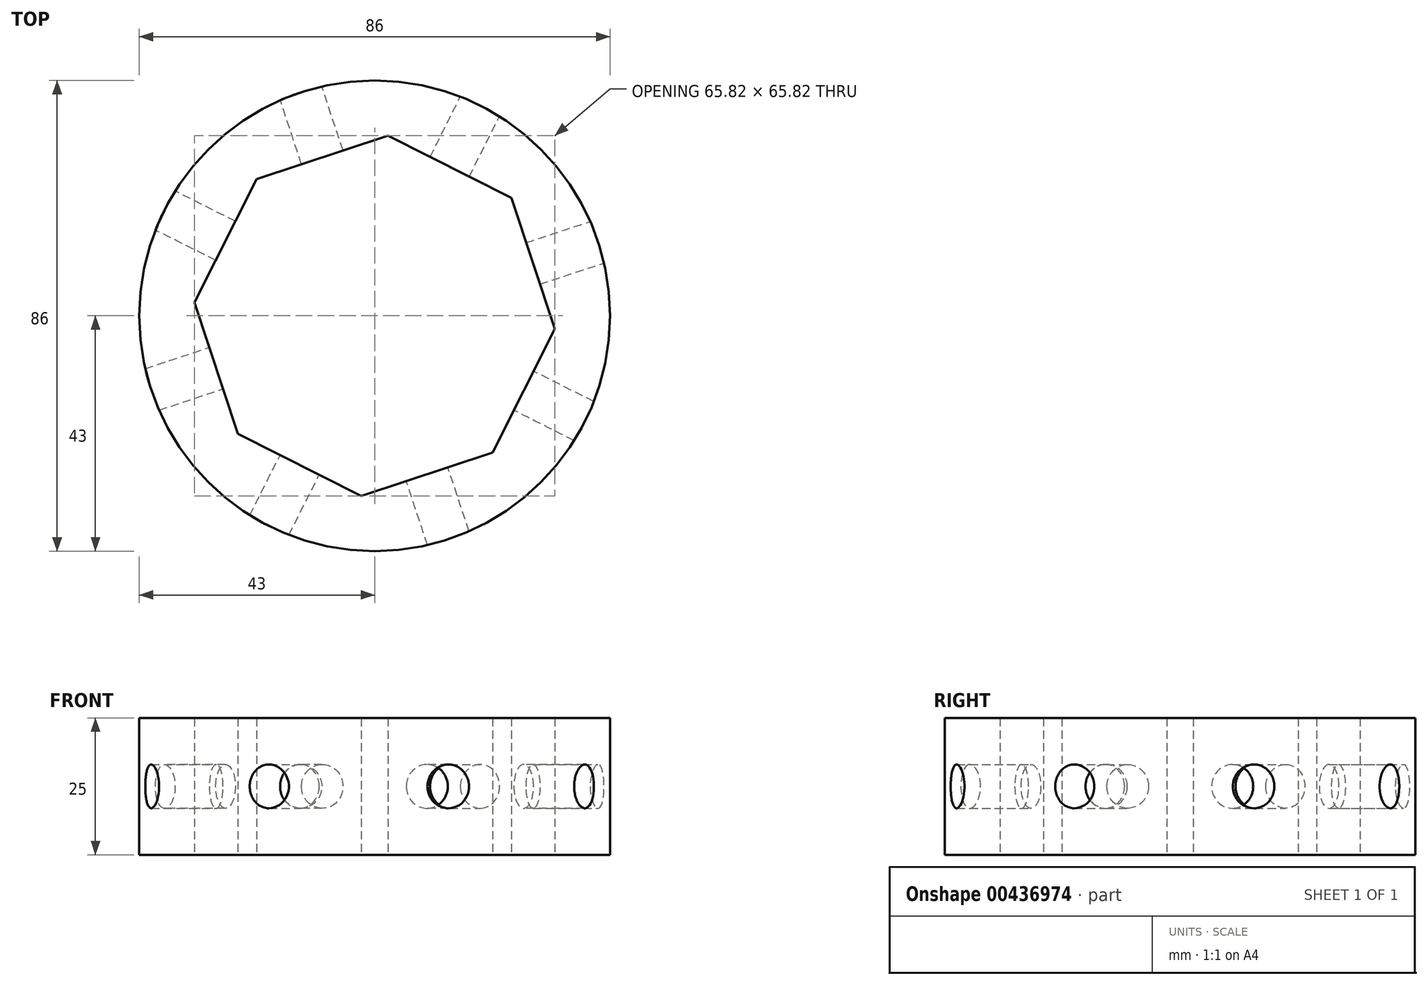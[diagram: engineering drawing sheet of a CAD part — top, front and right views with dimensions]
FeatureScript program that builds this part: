
annotation { "Feature Type Name" : "Feature", "Feature Type Description" : "" }
export const myFeature = defineFeature(function(context is Context, id is Id, definition is map)
    precondition{}
    {
        {
            var Q0;
            Q0=qCreatedBy(makeId("Top.planeOp"),FACE);
            var sketch = newSketch(context, id + "F0", { "sketchPlane" : qUnion([Q0])});
            skCircle(sketch, "E0", {"center": v(0, 0) * mm, "radius": 25 * mm, "construction": true});
            skCircle(sketch, "E1.cCircle", {"center": v(0, 0) * mm, "radius": 33 * mm, "construction": true});
            skLineSegment(sketch, "E1.0", {"start": v(-21.56, 24.98) * mm, "end": v(2.42, 32.91) * mm});
            skLineSegment(sketch, "E1.1", {"start": v(2.42, 32.91) * mm, "end": v(24.98, 21.56) * mm});
            skLineSegment(sketch, "E1.2", {"start": v(24.98, 21.56) * mm, "end": v(32.91, -2.42) * mm});
            skLineSegment(sketch, "E1.3", {"start": v(32.91, -2.42) * mm, "end": v(21.56, -24.98) * mm});
            skLineSegment(sketch, "E1.4", {"start": v(21.56, -24.98) * mm, "end": v(-2.42, -32.91) * mm});
            skLineSegment(sketch, "E1.5", {"start": v(-2.42, -32.91) * mm, "end": v(-24.98, -21.56) * mm});
            skLineSegment(sketch, "E1.6", {"start": v(-24.98, -21.56) * mm, "end": v(-32.91, 2.42) * mm});
            skLineSegment(sketch, "E1.7", {"start": v(-32.91, 2.42) * mm, "end": v(-21.56, 24.98) * mm});
            skCircle(sketch, "E2", {"center": v(0, 0) * mm, "radius": 43 * mm});
            skSolve(sketch);
        }
        {
            var Q0;
            Q0 = qSketchRegion(id + "F0", true);
            extrude(context, id + "F1", {"entities" : qUnion([Q0]), "depth" : 25 * mm, "offsetDistance" : 25 * mm});
        }
        {
            var Q0;
            Q0=makeQuery(id+"F1.opExtrude","SWEPT_FACE",FACE,{"disambiguationData":[OSD([sQuery(id+"F0.wireOp",EDGE,"E1.0")])]});
            var sketch = newSketch(context, id + "F2", { "sketchPlane" : qUnion([Q0])});
            skLineSegment(sketch, "E3.0.0", {"start": v(-12.63, 0) * mm, "end": v(12.63, 0) * mm, "construction": true});
            skLineSegment(sketch, "E3.0.1", {"start": v(12.63, 0) * mm, "end": v(12.63, 25) * mm, "construction": true});
            skLineSegment(sketch, "E3.0.2", {"start": v(12.63, 25) * mm, "end": v(-12.63, 25) * mm, "construction": true});
            skLineSegment(sketch, "E3.0.3", {"start": v(-12.63, 25) * mm, "end": v(-12.63, 0) * mm, "construction": true});
            skCircle(sketch, "E4", {"center": v(0, 12.5) * mm, "radius": 4 * mm});
            skPoint(sketch, "E4.centerSnap0", {"position": v(-12.63, 12.5) * mm});
            skPoint(sketch, "E4.centerSnap1", {"position": v(0, 25) * mm});
            skSolve(sketch);
        }
        {
            var Q0;
            Q0=makeQuery(id+"F1.opExtrude","SWEPT_FACE",FACE,{"disambiguationData":[OSD([sQuery(id+"F0.wireOp",EDGE,"E1.7")])]});
            var sketch = newSketch(context, id + "F3", { "sketchPlane" : qUnion([Q0])});
            skLineSegment(sketch, "E5.0.0", {"start": v(-12.63, 0) * mm, "end": v(12.63, 0) * mm, "construction": true});
            skLineSegment(sketch, "E5.0.1", {"start": v(12.63, 0) * mm, "end": v(12.63, 25) * mm, "construction": true});
            skLineSegment(sketch, "E5.0.2", {"start": v(12.63, 25) * mm, "end": v(-12.63, 25) * mm, "construction": true});
            skLineSegment(sketch, "E5.0.3", {"start": v(-12.63, 25) * mm, "end": v(-12.63, 0) * mm, "construction": true});
            skCircle(sketch, "E6", {"center": v(0, 12.5) * mm, "radius": 4 * mm});
            skPoint(sketch, "E6.centerSnap0", {"position": v(-12.63, 12.5) * mm});
            skPoint(sketch, "E6.centerSnap1", {"position": v(0, 25) * mm});
            skSolve(sketch);
        }
        {
            var Q0;
            Q0=makeQuery(id+"F1.opExtrude","SWEPT_FACE",FACE,{"disambiguationData":[OSD([sQuery(id+"F0.wireOp",EDGE,"E1.6")])]});
            var sketch = newSketch(context, id + "F4", { "sketchPlane" : qUnion([Q0])});
            skLineSegment(sketch, "E7.0.0", {"start": v(-12.63, 0) * mm, "end": v(12.63, 0) * mm, "construction": true});
            skLineSegment(sketch, "E7.0.1", {"start": v(12.63, 0) * mm, "end": v(12.63, 25) * mm, "construction": true});
            skLineSegment(sketch, "E7.0.2", {"start": v(12.63, 25) * mm, "end": v(-12.63, 25) * mm, "construction": true});
            skLineSegment(sketch, "E7.0.3", {"start": v(-12.63, 25) * mm, "end": v(-12.63, 0) * mm, "construction": true});
            skCircle(sketch, "E8", {"center": v(0, 12.5) * mm, "radius": 4 * mm});
            skPoint(sketch, "E8.centerSnap0", {"position": v(-12.63, 12.5) * mm});
            skPoint(sketch, "E8.centerSnap1", {"position": v(0, 25) * mm});
            skSolve(sketch);
        }
        {
            var Q0;
            Q0=makeQuery(id+"F1.opExtrude","SWEPT_FACE",FACE,{"disambiguationData":[OSD([sQuery(id+"F0.wireOp",EDGE,"E1.5")])]});
            var sketch = newSketch(context, id + "F5", { "sketchPlane" : qUnion([Q0])});
            skLineSegment(sketch, "E9.0.0", {"start": v(-12.63, 0) * mm, "end": v(12.63, 0) * mm, "construction": true});
            skLineSegment(sketch, "E9.0.1", {"start": v(12.63, 0) * mm, "end": v(12.63, 25) * mm, "construction": true});
            skLineSegment(sketch, "E9.0.2", {"start": v(12.63, 25) * mm, "end": v(-12.63, 25) * mm, "construction": true});
            skLineSegment(sketch, "E9.0.3", {"start": v(-12.63, 25) * mm, "end": v(-12.63, 0) * mm, "construction": true});
            skCircle(sketch, "E10", {"center": v(0, 12.5) * mm, "radius": 4 * mm});
            skPoint(sketch, "E10.centerSnap0", {"position": v(12.63, 12.5) * mm});
            skPoint(sketch, "E10.centerSnap1", {"position": v(0, 25) * mm});
            skSolve(sketch);
        }
        {
            var Q0;
            Q0 = qSketchRegion(id + "F5", true);
            extrude(context, id + "F6", {"entities" : qUnion([Q0]), "operationType" : NewBodyOperationType.REMOVE, "oppositeDirection" : true, "depth" : 20 * mm, "offsetDistance" : 25 * mm, "hasSecondDirection" : true, "secondDirectionOppositeDirection" : false, "secondDirectionDepth" : 79 * mm});
        }
        {
            var Q0;
            Q0 = qSketchRegion(id + "F4", true);
            extrude(context, id + "F7", {"entities" : qUnion([Q0]), "operationType" : NewBodyOperationType.REMOVE, "oppositeDirection" : true, "depth" : 20 * mm, "offsetDistance" : 25 * mm, "hasSecondDirection" : true, "secondDirectionOppositeDirection" : false, "secondDirectionDepth" : 80 * mm});
        }
        {
            var Q0;
            Q0 = qSketchRegion(id + "F3", true);
            extrude(context, id + "F8", {"entities" : qUnion([Q0]), "operationType" : NewBodyOperationType.REMOVE, "depth" : 93.1 * mm, "offsetDistance" : 25 * mm, "hasSecondDirection" : true, "secondDirectionOppositeDirection" : true, "secondDirectionDepth" : 25 * mm});
        }
        {
            var Q0;
            Q0 = qSketchRegion(id + "F2", true);
            extrude(context, id + "F9", {"entities" : qUnion([Q0]), "operationType" : NewBodyOperationType.REMOVE, "depth" : 82.3 * mm, "offsetDistance" : 25 * mm, "hasSecondDirection" : true, "secondDirectionOppositeDirection" : true, "secondDirectionDepth" : 25 * mm});
        }
    });
